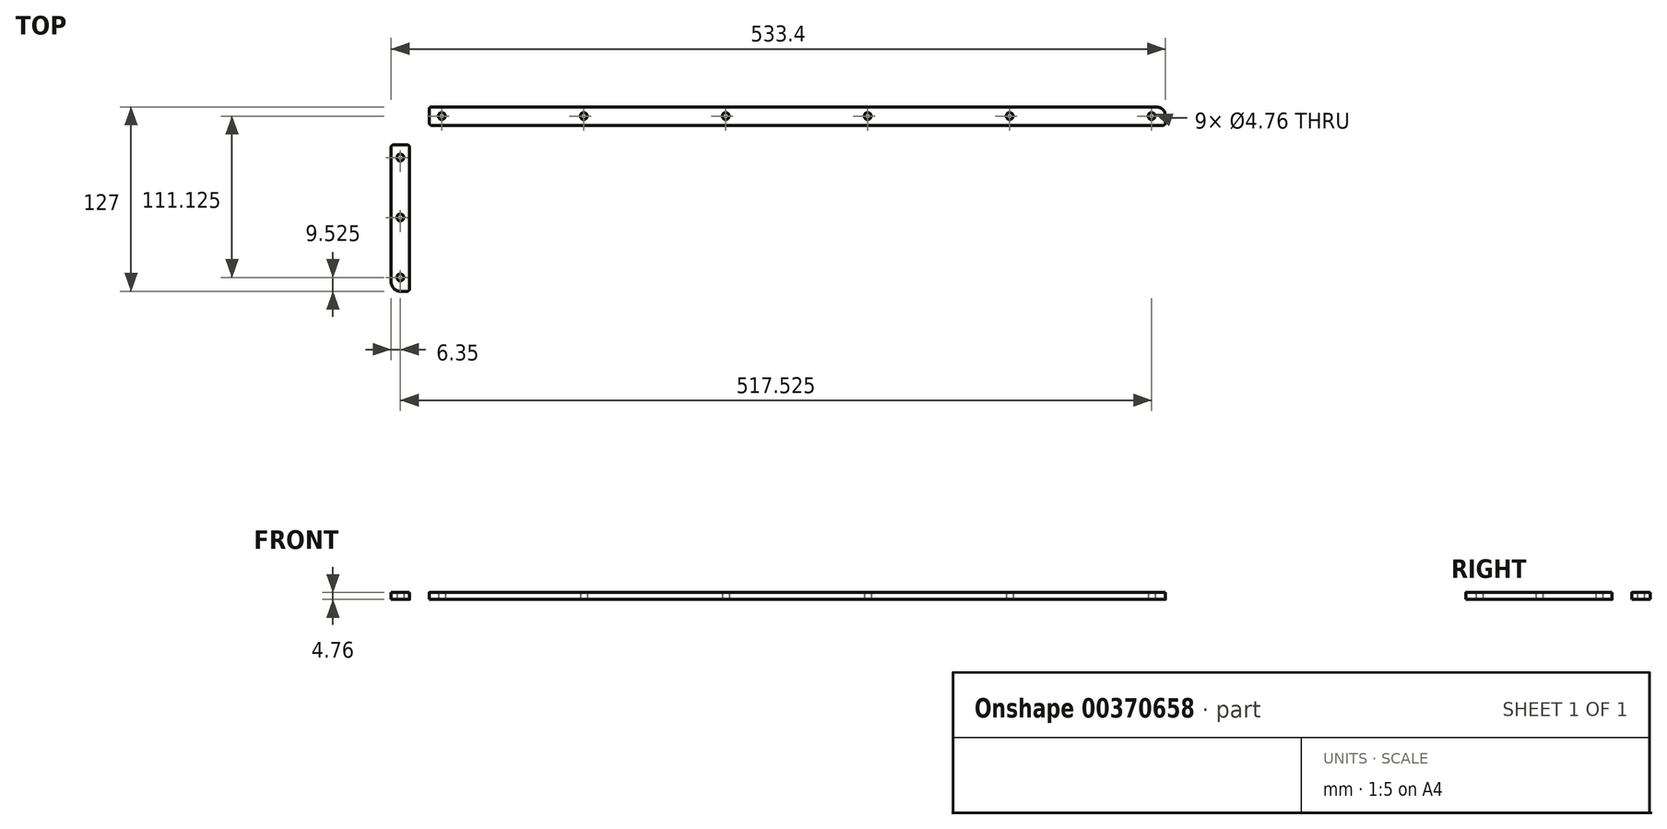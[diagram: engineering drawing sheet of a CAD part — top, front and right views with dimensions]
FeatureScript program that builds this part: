
annotation { "Feature Type Name" : "Feature", "Feature Type Description" : "" }
export const myFeature = defineFeature(function(context is Context, id is Id, definition is map)
    precondition{}
    {
        {
            var Q0;
            Q0=qCreatedBy(makeId("Top.planeOp"),FACE);
            var sketch = newSketch(context, id + "F0", { "sketchPlane" : qUnion([Q0])});
            skLineSegment(sketch, "E0.bottom", {"start": v(6.35, 0) * mm, "end": v(527.05, 0) * mm});
            skLineSegment(sketch, "E0.top", {"start": v(6.35, 127) * mm, "end": v(260.35, 127) * mm});
            skLineSegment(sketch, "E0.left", {"start": v(0, 6.35) * mm, "end": v(0, 120.65) * mm});
            skLineSegment(sketch, "E0.right", {"start": v(533.4, 6.35) * mm, "end": v(533.4, 120.65) * mm});
            skCircle(sketch, "E1", {"center": v(228.6, 95.25) * mm, "radius": 2.38 * mm});
            skCircle(sketch, "E2", {"center": v(228.6, 31.75) * mm, "radius": 2.38 * mm});
            skCircle(sketch, "E3", {"center": v(457.2, 95.25) * mm, "radius": 2.38 * mm});
            skCircle(sketch, "E4", {"center": v(457.2, 31.75) * mm, "radius": 2.38 * mm});
            skLineSegment(sketch, "E5", {"start": v(0, 114.3) * mm, "end": v(533.4, 114.3) * mm, "construction": true});
            skLineSegment(sketch, "E6.0", {"start": v(0, 101.6) * mm, "end": v(648.77, 101.6) * mm, "construction": true});
            skLineSegment(sketch, "E7.0", {"start": v(12.7, 0) * mm, "end": v(12.7, 127) * mm, "construction": true});
            skLineSegment(sketch, "E8.0", {"start": v(25.4, 0) * mm, "end": v(25.4, 127) * mm, "construction": true});
            skLineSegment(sketch, "E9.0", {"start": v(330.2, 127) * mm, "end": v(330.2, 267.26) * mm, "construction": true});
            skLineSegment(sketch, "E10.0", {"start": v(393.7, 133.35) * mm, "end": v(393.7, 152.4) * mm});
            skLineSegment(sketch, "E11.0", {"start": v(266.7, 133.35) * mm, "end": v(266.7, 152.4) * mm});
            skLineSegment(sketch, "E12.0", {"start": v(273.05, 158.75) * mm, "end": v(387.35, 158.75) * mm});
            skArc(sketch, "E13.filletArc", {"start": v(273.05, 158.75) * mm, "mid": v(268.56, 156.9) * mm, "end": v(266.7, 152.4) * mm});
            skLineSegment(sketch, "E14.trimOffspring", {"start": v(400.05, 127) * mm, "end": v(527.05, 127) * mm});
            skPoint(sketch, "E15.visualSharp", {"position": v(266.7, 127) * mm});
            skArc(sketch, "E15.filletArc", {"start": v(260.35, 127) * mm, "mid": v(264.84, 128.86) * mm, "end": v(266.7, 133.35) * mm});
            skArc(sketch, "E16.filletArc", {"start": v(393.7, 152.4) * mm, "mid": v(391.84, 156.9) * mm, "end": v(387.35, 158.75) * mm});
            skPoint(sketch, "E17.visualSharp", {"position": v(393.7, 127) * mm});
            skArc(sketch, "E17.filletArc", {"start": v(393.7, 133.35) * mm, "mid": v(395.56, 128.86) * mm, "end": v(400.05, 127) * mm});
            skCircle(sketch, "E18", {"center": v(307.98, 147.64) * mm, "radius": 2.38 * mm});
            skCircle(sketch, "E19", {"center": v(352.42, 147.64) * mm, "radius": 2.38 * mm});
            skLineSegment(sketch, "E20", {"start": v(307.98, 147.64) * mm, "end": v(352.42, 147.64) * mm, "construction": true});
            skPoint(sketch, "E21", {"position": v(330.2, 147.64) * mm});
            skPoint(sketch, "E22.visualSharp", {"position": v(0, 127) * mm});
            skArc(sketch, "E22.filletArc", {"start": v(6.35, 127) * mm, "mid": v(1.86, 125.14) * mm, "end": v(0, 120.65) * mm});
            skPoint(sketch, "E23.visualSharp", {"position": v(0, 0) * mm});
            skArc(sketch, "E23.filletArc", {"start": v(0, 6.35) * mm, "mid": v(1.86, 1.86) * mm, "end": v(6.35, 0) * mm});
            skPoint(sketch, "E24.visualSharp", {"position": v(533.4, 0) * mm});
            skArc(sketch, "E24.filletArc", {"start": v(527.05, 0) * mm, "mid": v(531.54, 1.86) * mm, "end": v(533.4, 6.35) * mm});
            skPoint(sketch, "E25.visualSharp", {"position": v(533.4, 127) * mm});
            skArc(sketch, "E25.filletArc", {"start": v(533.4, 120.65) * mm, "mid": v(531.54, 125.14) * mm, "end": v(527.05, 127) * mm});
            skCircle(sketch, "E26", {"center": v(6.35, 9.53) * mm, "radius": 2.38 * mm});
            skCircle(sketch, "E27", {"center": v(6.35, 50.8) * mm, "radius": 2.38 * mm});
            skCircle(sketch, "E28", {"center": v(6.35, 92.08) * mm, "radius": 2.38 * mm});
            skCircle(sketch, "E29", {"center": v(34.92, 120.65) * mm, "radius": 2.38 * mm});
            skCircle(sketch, "E30", {"center": v(132.72, 120.65) * mm, "radius": 2.38 * mm});
            skCircle(sketch, "E31", {"center": v(230.5, 120.65) * mm, "radius": 2.38 * mm});
            skCircle(sketch, "E32", {"center": v(328.3, 120.65) * mm, "radius": 2.38 * mm});
            skCircle(sketch, "E33", {"center": v(426.09, 120.65) * mm, "radius": 2.38 * mm});
            skCircle(sketch, "E34", {"center": v(523.88, 120.65) * mm, "radius": 2.38 * mm});
            skLineSegment(sketch, "E35", {"start": v(34.92, 120.65) * mm, "end": v(132.72, 120.65) * mm, "construction": true});
            skLineSegment(sketch, "E36", {"start": v(132.72, 120.65) * mm, "end": v(230.5, 120.65) * mm, "construction": true});
            skLineSegment(sketch, "E37", {"start": v(230.5, 120.65) * mm, "end": v(328.3, 120.65) * mm, "construction": true});
            skLineSegment(sketch, "E38", {"start": v(328.3, 120.65) * mm, "end": v(426.09, 120.65) * mm, "construction": true});
            skLineSegment(sketch, "E39", {"start": v(426.09, 120.65) * mm, "end": v(523.88, 120.65) * mm, "construction": true});
            skLineSegment(sketch, "E40", {"start": v(6.35, 92.08) * mm, "end": v(6.35, 50.8) * mm, "construction": true});
            skLineSegment(sketch, "E41", {"start": v(6.35, 50.8) * mm, "end": v(6.35, 9.53) * mm, "construction": true});
            skLineSegment(sketch, "E42.bottom", {"start": v(260.35, 114.3) * mm, "end": v(400.05, 114.3) * mm});
            skLineSegment(sketch, "E42.top", {"start": v(260.35, 63.5) * mm, "end": v(400.05, 63.5) * mm});
            skLineSegment(sketch, "E42.left", {"start": v(254, 107.95) * mm, "end": v(254, 69.85) * mm});
            skLineSegment(sketch, "E42.right", {"start": v(406.4, 107.95) * mm, "end": v(406.4, 69.85) * mm});
            skPoint(sketch, "E43.visualSharp", {"position": v(254, 114.3) * mm});
            skArc(sketch, "E43.filletArc", {"start": v(260.35, 114.3) * mm, "mid": v(255.86, 112.44) * mm, "end": v(254, 107.95) * mm});
            skPoint(sketch, "E44.visualSharp", {"position": v(254, 63.5) * mm});
            skArc(sketch, "E44.filletArc", {"start": v(254, 69.85) * mm, "mid": v(255.86, 65.36) * mm, "end": v(260.35, 63.5) * mm});
            skPoint(sketch, "E45.visualSharp", {"position": v(406.4, 63.5) * mm});
            skArc(sketch, "E45.filletArc", {"start": v(400.05, 63.5) * mm, "mid": v(404.54, 65.36) * mm, "end": v(406.4, 69.85) * mm});
            skPoint(sketch, "E46.visualSharp", {"position": v(406.4, 114.3) * mm});
            skArc(sketch, "E46.filletArc", {"start": v(406.4, 107.95) * mm, "mid": v(404.54, 112.44) * mm, "end": v(400.05, 114.3) * mm});
            skSolve(sketch);
        }
        {
            var Q0;
            Q0=qSketchRegion(id+"F0",true);
            extrude(context, id + "F1", {"entities" : qUnion([Q0]), "depth" : 4.76 * mm});
        }
        {
            var Q0;
            Q0=makeQuery(id+"F1.opExtrude","CAP_FACE",FACE,{"disambiguationData":[OSD([sQuery(id+"F0.wireOp",EDGE,"E0.bottom"),sQuery(id+"F0.wireOp",EDGE,"E0.top"),sQuery(id+"F0.wireOp",EDGE,"E0.left"),sQuery(id+"F0.wireOp",EDGE,"E0.right"),sQuery(id+"F0.wireOp",EDGE,"E1"),sQuery(id+"F0.wireOp",EDGE,"E2"),sQuery(id+"F0.wireOp",EDGE,"E3"),sQuery(id+"F0.wireOp",EDGE,"E4"),sQuery(id+"F0.wireOp",EDGE,"E10.0"),sQuery(id+"F0.wireOp",EDGE,"E11.0"),sQuery(id+"F0.wireOp",EDGE,"E12.0"),sQuery(id+"F0.wireOp",EDGE,"E13.filletArc"),sQuery(id+"F0.wireOp",EDGE,"E14.trimOffspring"),sQuery(id+"F0.wireOp",EDGE,"E15.filletArc"),sQuery(id+"F0.wireOp",EDGE,"E16.filletArc"),sQuery(id+"F0.wireOp",EDGE,"E17.filletArc"),sQuery(id+"F0.wireOp",EDGE,"E18"),sQuery(id+"F0.wireOp",EDGE,"8vzgHWK5-CGjt-0HD0-FSng-8EKi4hqDK3IT"),sQuery(id+"F0.wireOp",EDGE,"UmFmnjl2-O3XH-EXjj-iWft-K4RkXt2c9gUR"),sQuery(id+"F0.wireOp",EDGE,"E19"),sQuery(id+"F0.wireOp",EDGE,"E22.filletArc"),sQuery(id+"F0.wireOp",EDGE,"E23.filletArc"),sQuery(id+"F0.wireOp",EDGE,"E24.filletArc"),sQuery(id+"F0.wireOp",EDGE,"E25.filletArc"),sQuery(id+"F0.wireOp",EDGE,"E26"),sQuery(id+"F0.wireOp",EDGE,"E27"),sQuery(id+"F0.wireOp",EDGE,"E28"),sQuery(id+"F0.wireOp",EDGE,"E29"),sQuery(id+"F0.wireOp",EDGE,"E30"),sQuery(id+"F0.wireOp",EDGE,"E31"),sQuery(id+"F0.wireOp",EDGE,"E32"),sQuery(id+"F0.wireOp",EDGE,"E33"),sQuery(id+"F0.wireOp",EDGE,"E34")])],"isStart":false});
            var sketch = newSketch(context, id + "F2", { "sketchPlane" : qUnion([Q0])});
            skText(sketch, "E47", { "text": "STANLEY\nD-4550 & D-4551\nREGULAR ARM\nPULL SIDE\nTHIS SIDE LEFT HAND", "fontName": "NotoSansCJKjp-Regular.otf"});
            const initialGuessF2  = {"E47": [0.05559, 0.08436, 1, 0, 0.01089]};
            skSetInitialGuess(sketch, initialGuessF2);
            skSolve(sketch);
        }
        {
            var Q0;
            Q0=qSketchRegion(id+"F2",true);
            extrude(context, id + "F3", {"entities" : qUnion([Q0]), "operationType" : NewBodyOperationType.REMOVE, "oppositeDirection" : true, "depth" : 0.8 * mm});
        }
        {
            var Q0;
            {var subQ0=sQuery(id+"F0.wireOp",EDGE,"E42.bottom");var subQ1=sQuery(id+"F0.wireOp",EDGE,"E26");var subQ2=sQuery(id+"F0.wireOp",EDGE,"E25.filletArc");var subQ3=sQuery(id+"F0.wireOp",EDGE,"E24.filletArc");var subQ4=sQuery(id+"F0.wireOp",EDGE,"E23.filletArc");var subQ5=sQuery(id+"F0.wireOp",EDGE,"E22.filletArc");var subQ6=sQuery(id+"F0.wireOp",EDGE,"E17.filletArc");var subQ7=sQuery(id+"F0.wireOp",EDGE,"E16.filletArc");var subQ8=sQuery(id+"F0.wireOp",EDGE,"E15.filletArc");var subQ9=sQuery(id+"F0.wireOp",EDGE,"E14.trimOffspring");var subQ10=sQuery(id+"F0.wireOp",EDGE,"E13.filletArc");var subQ11=sQuery(id+"F0.wireOp",EDGE,"E12.0");var subQ12=sQuery(id+"F0.wireOp",EDGE,"E11.0");var subQ13=sQuery(id+"F0.wireOp",EDGE,"E10.0");var subQ14=sQuery(id+"F0.wireOp",EDGE,"E4");var subQ15=sQuery(id+"F0.wireOp",EDGE,"E3");var subQ16=sQuery(id+"F0.wireOp",EDGE,"E0.right");var subQ17=sQuery(id+"F0.wireOp",EDGE,"E0.left");var subQ18=sQuery(id+"F0.wireOp",EDGE,"E0.top");var subQ19=sQuery(id+"F0.wireOp",EDGE,"E0.bottom");var subQ20=sQuery(id+"F0.wireOp",EDGE,"E19");var subQ21=sQuery(id+"F0.wireOp",EDGE,"E42.left");var subQ22=sQuery(id+"F0.wireOp",EDGE,"E42.top");var subQ23=sQuery(id+"F0.wireOp",EDGE,"E42.right");var subQ24=sQuery(id+"F0.wireOp",EDGE,"E43.filletArc");var subQ25=sQuery(id+"F0.wireOp",EDGE,"E1");var subQ26=sQuery(id+"F0.wireOp",EDGE,"E44.filletArc");var subQ27=sQuery(id+"F0.wireOp",EDGE,"E2");var subQ28=sQuery(id+"F0.wireOp",EDGE,"E45.filletArc");var subQ29=sQuery(id+"F0.wireOp",EDGE,"E46.filletArc");var subQ30=sQuery(id+"F0.wireOp",EDGE,"E29");var subQ31=sQuery(id+"F0.wireOp",EDGE,"E30");var subQ32=sQuery(id+"F0.wireOp",EDGE,"E18");var subQ33=sQuery(id+"F0.wireOp",EDGE,"E31");var subQ34=sQuery(id+"F0.wireOp",EDGE,"E32");var subQ35=sQuery(id+"F0.wireOp",EDGE,"E33");var subQ36=sQuery(id+"F0.wireOp",EDGE,"E34");var subQ37=sQuery(id+"F0.wireOp",EDGE,"E27");var subQ38=sQuery(id+"F0.wireOp",EDGE,"E28");Q0=makeQuery(id+"F3.boolean.opBoolean","SPLIT",FACE,{"disambiguationData":[TD([makeQuery(id+"F1.opExtrude","SWEPT_FACE",FACE,{"disambiguationData":[OSD([subQ19])]})])],"derivedFrom":makeQuery(id+"F1.opExtrude","CAP_FACE",FACE,{"disambiguationData":[OSD([subQ19,subQ18,subQ17,subQ16,subQ25,subQ27,subQ15,subQ14,subQ13,subQ12,subQ11,subQ10,subQ9,subQ8,subQ7,subQ6,subQ32,subQ20,subQ5,subQ4,subQ3,subQ2,subQ1,subQ37,subQ38,subQ30,subQ31,subQ33,subQ34,subQ35,subQ36,subQ0,subQ22,subQ21,subQ23,subQ24,subQ26,subQ28,subQ29])],"isStart":false})});}
            var sketch = newSketch(context, id + "F4", { "sketchPlane" : qUnion([Q0])});
            skLineSegment(sketch, "E48.bottom", {"start": v(0, 127) * mm, "end": v(26.2, 127) * mm});
            skLineSegment(sketch, "E48.top", {"start": v(0, 100.8) * mm, "end": v(26.2, 100.8) * mm});
            skLineSegment(sketch, "E48.left", {"start": v(0, 127) * mm, "end": v(0, 100.8) * mm});
            skLineSegment(sketch, "E48.right", {"start": v(26.2, 127) * mm, "end": v(26.2, 100.8) * mm});
            skLineSegment(sketch, "E49.bottom", {"start": v(533.4, 0) * mm, "end": v(12.7, 0) * mm});
            skLineSegment(sketch, "E49.top", {"start": v(533.4, 114.3) * mm, "end": v(12.7, 114.3) * mm});
            skLineSegment(sketch, "E49.left", {"start": v(533.4, 0) * mm, "end": v(533.4, 114.3) * mm});
            skLineSegment(sketch, "E49.right", {"start": v(12.7, 0) * mm, "end": v(12.7, 114.3) * mm});
            skLineSegment(sketch, "E50.bottom", {"start": v(260.35, 165.1) * mm, "end": v(400.05, 165.1) * mm});
            skLineSegment(sketch, "E50.top", {"start": v(260.35, 127) * mm, "end": v(400.05, 127) * mm});
            skLineSegment(sketch, "E50.left", {"start": v(260.35, 165.1) * mm, "end": v(260.35, 127) * mm});
            skLineSegment(sketch, "E50.right", {"start": v(400.05, 165.1) * mm, "end": v(400.05, 127) * mm});
            skSolve(sketch);
        }
        {
            var Q0;
            Q0 = qSketchRegion(id + "F4", true);
            extrude(context, id + "F5", {"entities" : qUnion([Q0]), "operationType" : NewBodyOperationType.REMOVE, "endBound" : BoundingType.THROUGH_ALL, "oppositeDirection" : true, "depth" : 25.4 * mm});
        }
        {
            var Q0;
            {var subQ0=sQuery(id+"F0.wireOp",EDGE,"E23.filletArc");var subQ2=sQuery(id+"F0.wireOp",EDGE,"E26");var subQ4=sQuery(id+"F0.wireOp",EDGE,"E0.left");var subQ6=sQuery(id+"F0.wireOp",EDGE,"E28");var subQ8=sQuery(id+"F0.wireOp",EDGE,"E0.bottom");var subQ9=makeQuery(id+"F1.opExtrude","SWEPT_FACE",FACE,{"disambiguationData":[OSD([subQ8])]});var subQ10=sQuery(id+"F0.wireOp",EDGE,"E27");var subQ12=sQuery(id+"F0.wireOp",EDGE,"E42.bottom");var subQ13=sQuery(id+"F0.wireOp",EDGE,"E25.filletArc");var subQ14=sQuery(id+"F0.wireOp",EDGE,"E24.filletArc");var subQ15=sQuery(id+"F0.wireOp",EDGE,"E22.filletArc");var subQ16=sQuery(id+"F0.wireOp",EDGE,"E17.filletArc");var subQ17=sQuery(id+"F0.wireOp",EDGE,"E16.filletArc");var subQ18=sQuery(id+"F0.wireOp",EDGE,"E15.filletArc");var subQ19=sQuery(id+"F0.wireOp",EDGE,"E14.trimOffspring");var subQ20=sQuery(id+"F0.wireOp",EDGE,"E13.filletArc");var subQ21=sQuery(id+"F0.wireOp",EDGE,"E12.0");var subQ22=sQuery(id+"F0.wireOp",EDGE,"E11.0");var subQ23=sQuery(id+"F0.wireOp",EDGE,"E10.0");var subQ24=sQuery(id+"F0.wireOp",EDGE,"E4");var subQ25=sQuery(id+"F0.wireOp",EDGE,"E3");var subQ26=sQuery(id+"F0.wireOp",EDGE,"E0.right");var subQ27=sQuery(id+"F0.wireOp",EDGE,"E0.top");var subQ28=sQuery(id+"F0.wireOp",EDGE,"E19");var subQ29=sQuery(id+"F0.wireOp",EDGE,"E42.left");var subQ30=sQuery(id+"F0.wireOp",EDGE,"E42.top");var subQ31=sQuery(id+"F0.wireOp",EDGE,"E42.right");var subQ32=sQuery(id+"F0.wireOp",EDGE,"E43.filletArc");var subQ33=sQuery(id+"F0.wireOp",EDGE,"E1");var subQ34=sQuery(id+"F0.wireOp",EDGE,"E44.filletArc");var subQ35=sQuery(id+"F0.wireOp",EDGE,"E2");var subQ36=sQuery(id+"F0.wireOp",EDGE,"E45.filletArc");var subQ37=sQuery(id+"F0.wireOp",EDGE,"E46.filletArc");var subQ38=sQuery(id+"F0.wireOp",EDGE,"E29");var subQ39=sQuery(id+"F0.wireOp",EDGE,"E30");var subQ40=sQuery(id+"F0.wireOp",EDGE,"E18");var subQ41=sQuery(id+"F0.wireOp",EDGE,"E31");var subQ42=sQuery(id+"F0.wireOp",EDGE,"E32");var subQ43=sQuery(id+"F0.wireOp",EDGE,"E33");var subQ44=sQuery(id+"F0.wireOp",EDGE,"E34");Q0=makeQuery(id+"F5.boolean.opBoolean","SPLIT",FACE,{"disambiguationData":[TD([subQ9])],"derivedFrom":makeQuery(id+"F3.boolean.opBoolean","SPLIT",FACE,{"disambiguationData":[TD([subQ9])],"derivedFrom":makeQuery(id+"F1.opExtrude","CAP_FACE",FACE,{"disambiguationData":[OSD([subQ8,subQ27,subQ4,subQ26,subQ33,subQ35,subQ25,subQ24,subQ23,subQ22,subQ21,subQ20,subQ19,subQ18,subQ17,subQ16,subQ40,subQ28,subQ15,subQ0,subQ14,subQ13,subQ2,subQ10,subQ6,subQ38,subQ39,subQ41,subQ42,subQ43,subQ44,subQ12,subQ30,subQ29,subQ31,subQ32,subQ34,subQ36,subQ37])],"isStart":false})})});}
            var sketch = newSketch(context, id + "F6", { "sketchPlane" : qUnion([Q0])});
            skLineSegment(sketch, "E51.0.0", {"start": v(12.7, 100.8) * mm, "end": v(11.11, 100.8) * mm});
            skLineSegment(sketch, "E51.0.1", {"start": v(0, 100.8) * mm, "end": v(0, 99.22) * mm});
            skLineSegment(sketch, "E51.0.3", {"start": v(11.11, 0) * mm, "end": v(12.7, 0) * mm});
            skLineSegment(sketch, "E51.0.4", {"start": v(12.7, 0) * mm, "end": v(12.7, 1.59) * mm});
            skLineSegment(sketch, "E52.0.1", {"start": v(27.78, 127) * mm, "end": v(26.2, 127) * mm});
            skLineSegment(sketch, "E52.0.2", {"start": v(26.2, 127) * mm, "end": v(26.2, 125.41) * mm});
            skLineSegment(sketch, "E52.0.3", {"start": v(26.2, 114.3) * mm, "end": v(27.78, 114.3) * mm});
            skLineSegment(sketch, "E52.0.4", {"start": v(533.4, 114.3) * mm, "end": v(533.4, 115.89) * mm});
            skPoint(sketch, "E53.visualSharp", {"position": v(533.4, 114.3) * mm});
            skArc(sketch, "E53.filletArc", {"start": v(531.81, 114.3) * mm, "mid": v(532.94, 114.76) * mm, "end": v(533.4, 115.89) * mm});
            skPoint(sketch, "E54.visualSharp", {"position": v(26.2, 127) * mm});
            skArc(sketch, "E54.filletArc", {"start": v(27.78, 127) * mm, "mid": v(26.66, 126.54) * mm, "end": v(26.2, 125.41) * mm});
            skPoint(sketch, "E55.visualSharp", {"position": v(26.2, 114.3) * mm});
            skArc(sketch, "E55.filletArc", {"start": v(26.2, 115.89) * mm, "mid": v(26.66, 114.76) * mm, "end": v(27.78, 114.3) * mm});
            skPoint(sketch, "E56.visualSharp", {"position": v(0, 100.8) * mm});
            skArc(sketch, "E56.filletArc", {"start": v(1.59, 100.8) * mm, "mid": v(0.46, 100.34) * mm, "end": v(0, 99.22) * mm});
            skPoint(sketch, "E57.visualSharp", {"position": v(12.7, 100.8) * mm});
            skArc(sketch, "E57.filletArc", {"start": v(12.7, 99.22) * mm, "mid": v(12.24, 100.34) * mm, "end": v(11.11, 100.8) * mm});
            skPoint(sketch, "E58.visualSharp", {"position": v(12.7, 0) * mm});
            skArc(sketch, "E58.filletArc", {"start": v(11.11, 0) * mm, "mid": v(12.24, 0.46) * mm, "end": v(12.7, 1.59) * mm});
            skPoint(sketch, "E59.orphan", {"position": v(533.4, 120.65) * mm});
            skLineSegment(sketch, "E60.trimOffspring", {"start": v(531.81, 114.3) * mm, "end": v(533.4, 114.3) * mm});
            skPoint(sketch, "E61.orphan", {"position": v(527.05, 127) * mm});
            skLineSegment(sketch, "E62.trimOffspring", {"start": v(26.2, 115.89) * mm, "end": v(26.2, 114.3) * mm});
            skPoint(sketch, "E63.orphan", {"position": v(0, 6.35) * mm});
            skLineSegment(sketch, "E64.trimOffspring", {"start": v(1.59, 100.8) * mm, "end": v(0, 100.8) * mm});
            skLineSegment(sketch, "E65.trimOffspring", {"start": v(12.7, 99.22) * mm, "end": v(12.7, 100.8) * mm});
            skPoint(sketch, "E66.orphan", {"position": v(6.35, 0) * mm});
            skSolve(sketch);
        }
        {
            var Q0;
            Q0 = qSketchRegion(id + "F6", true);
            extrude(context, id + "F7", {"entities" : qUnion([Q0]), "operationType" : NewBodyOperationType.REMOVE, "endBound" : BoundingType.UP_TO_NEXT, "oppositeDirection" : true, "depth" : 25.4 * mm});
        }
    });
